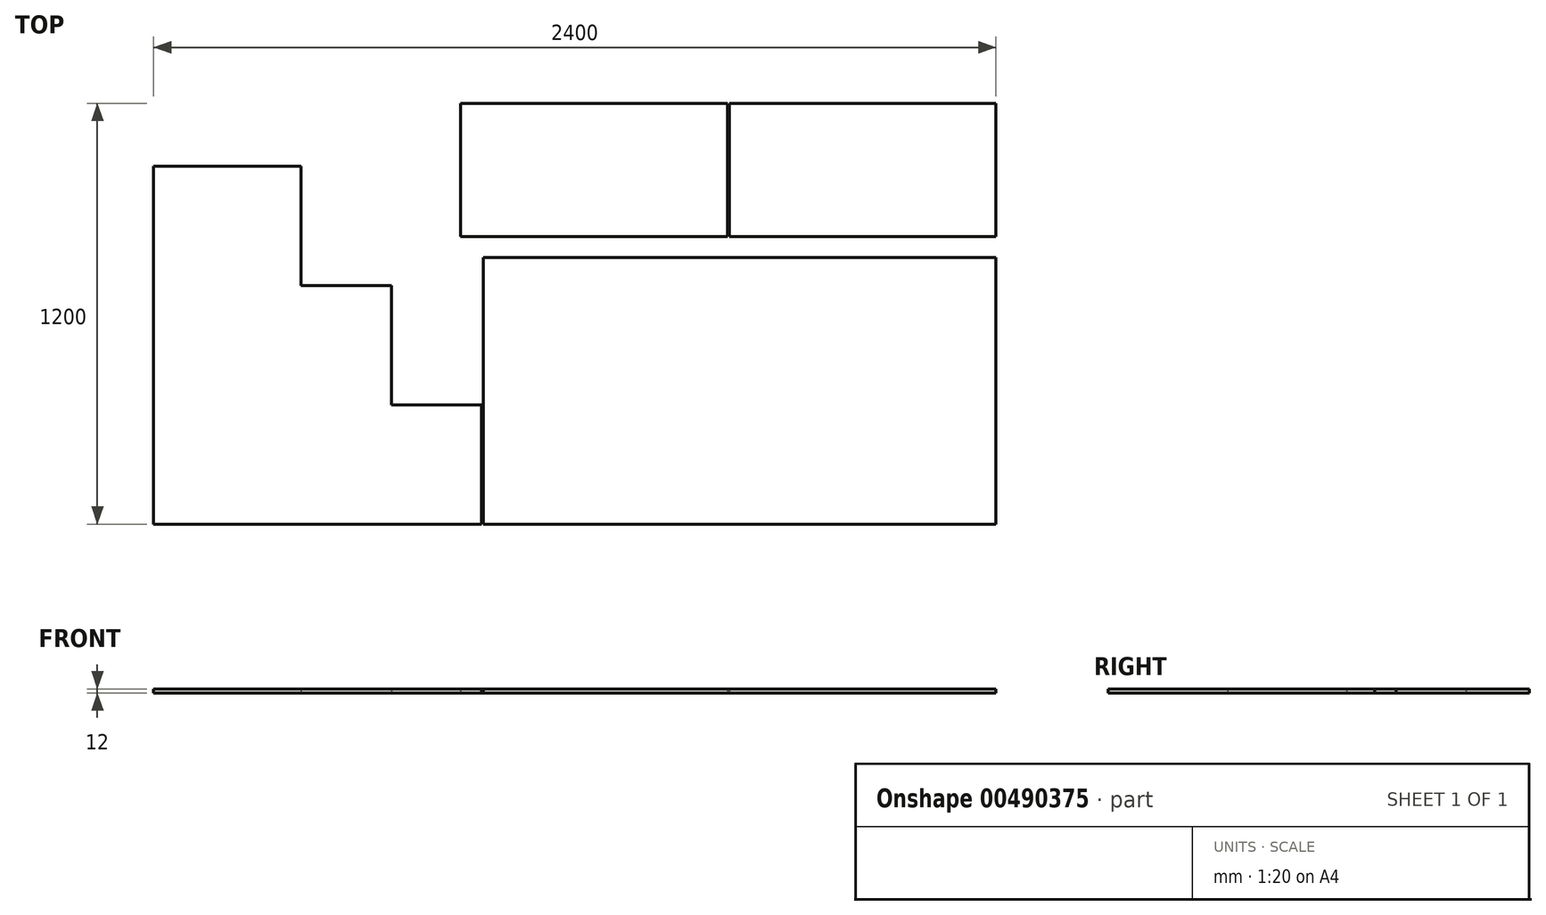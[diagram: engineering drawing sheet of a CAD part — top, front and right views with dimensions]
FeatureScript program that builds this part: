
annotation { "Feature Type Name" : "Feature", "Feature Type Description" : "" }
export const myFeature = defineFeature(function(context is Context, id is Id, definition is map)
    precondition{}
    {
        {
            var Q0;
            Q0=qCreatedBy(makeId("Top.planeOp"),FACE);
            var sketch = newSketch(context, id + "F0", { "sketchPlane" : qUnion([Q0])});
            skLineSegment(sketch, "E0.bottom", {"start": v(0, 0) * mm, "end": v(2400, 0) * mm});
            skLineSegment(sketch, "E0.top", {"start": v(0, 1200) * mm, "end": v(2400, 1200) * mm});
            skLineSegment(sketch, "E0.left", {"start": v(0, 0) * mm, "end": v(0, 1200) * mm});
            skLineSegment(sketch, "E0.right", {"start": v(2400, 0) * mm, "end": v(2400, 1200) * mm});
            skLineSegment(sketch, "E1", {"start": v(935, 0) * mm, "end": v(935, 340) * mm});
            skLineSegment(sketch, "E2", {"start": v(935, 340) * mm, "end": v(677.5, 340) * mm});
            skLineSegment(sketch, "E3", {"start": v(677.5, 340) * mm, "end": v(677.5, 680) * mm});
            skLineSegment(sketch, "E4", {"start": v(677.5, 680) * mm, "end": v(420, 680) * mm});
            skLineSegment(sketch, "E5", {"start": v(420, 680) * mm, "end": v(420, 1020) * mm});
            skLineSegment(sketch, "E6", {"start": v(420, 1020) * mm, "end": v(0, 1020) * mm});
            skLineSegment(sketch, "E7", {"start": v(2400, 820) * mm, "end": v(1640, 820) * mm});
            skLineSegment(sketch, "E8", {"start": v(1640, 820) * mm, "end": v(1640, 1200) * mm});
            skLineSegment(sketch, "E9", {"start": v(2400, 760) * mm, "end": v(940, 760) * mm});
            skLineSegment(sketch, "E10", {"start": v(940, 760) * mm, "end": v(940, 0) * mm});
            skLineSegment(sketch, "E11", {"start": v(1635, 1200) * mm, "end": v(1635, 820) * mm});
            skLineSegment(sketch, "E12", {"start": v(1635, 820) * mm, "end": v(875, 820) * mm});
            skLineSegment(sketch, "E13", {"start": v(875, 820) * mm, "end": v(875, 1200) * mm});
            skSolve(sketch);
        }
        {
            var Q0;
            {var subQ0=sQuery(id+"F0.wireOp",EDGE,"E1");Q0=makeQuery(id+"F0.imprint","IMPRINT",FACE,{"disambiguationData":[TD([[makeQuery(id+"F0.imprint","IMPRINT",EDGE,{"derivedFrom":subQ0}),1.0]])]});}
            var Q1;
            {var subQ4=sQuery(id+"F0.wireOp",EDGE,"E9");Q1=makeQuery(id+"F0.imprint","IMPRINT",FACE,{"disambiguationData":[TD([[makeQuery(id+"F0.imprint","IMPRINT",EDGE,{"derivedFrom":subQ4}),1.0]])]});}
            var Q2;
            {var subQ0=sQuery(id+"F0.wireOp",EDGE,"E11");Q2=makeQuery(id+"F0.imprint","IMPRINT",FACE,{"disambiguationData":[TD([[makeQuery(id+"F0.imprint","IMPRINT",EDGE,{"derivedFrom":subQ0}),-1.0]])]});}
            var Q3;
            {var subQ4=sQuery(id+"F0.wireOp",EDGE,"E7");Q3=makeQuery(id+"F0.imprint","IMPRINT",FACE,{"disambiguationData":[TD([[makeQuery(id+"F0.imprint","IMPRINT",EDGE,{"derivedFrom":subQ4}),-1.0]])]});}
            extrude(context, id + "F1", {"entities" : qUnion([Q0, Q1, Q2, Q3]), "depth" : 12 * mm});
        }
    });
